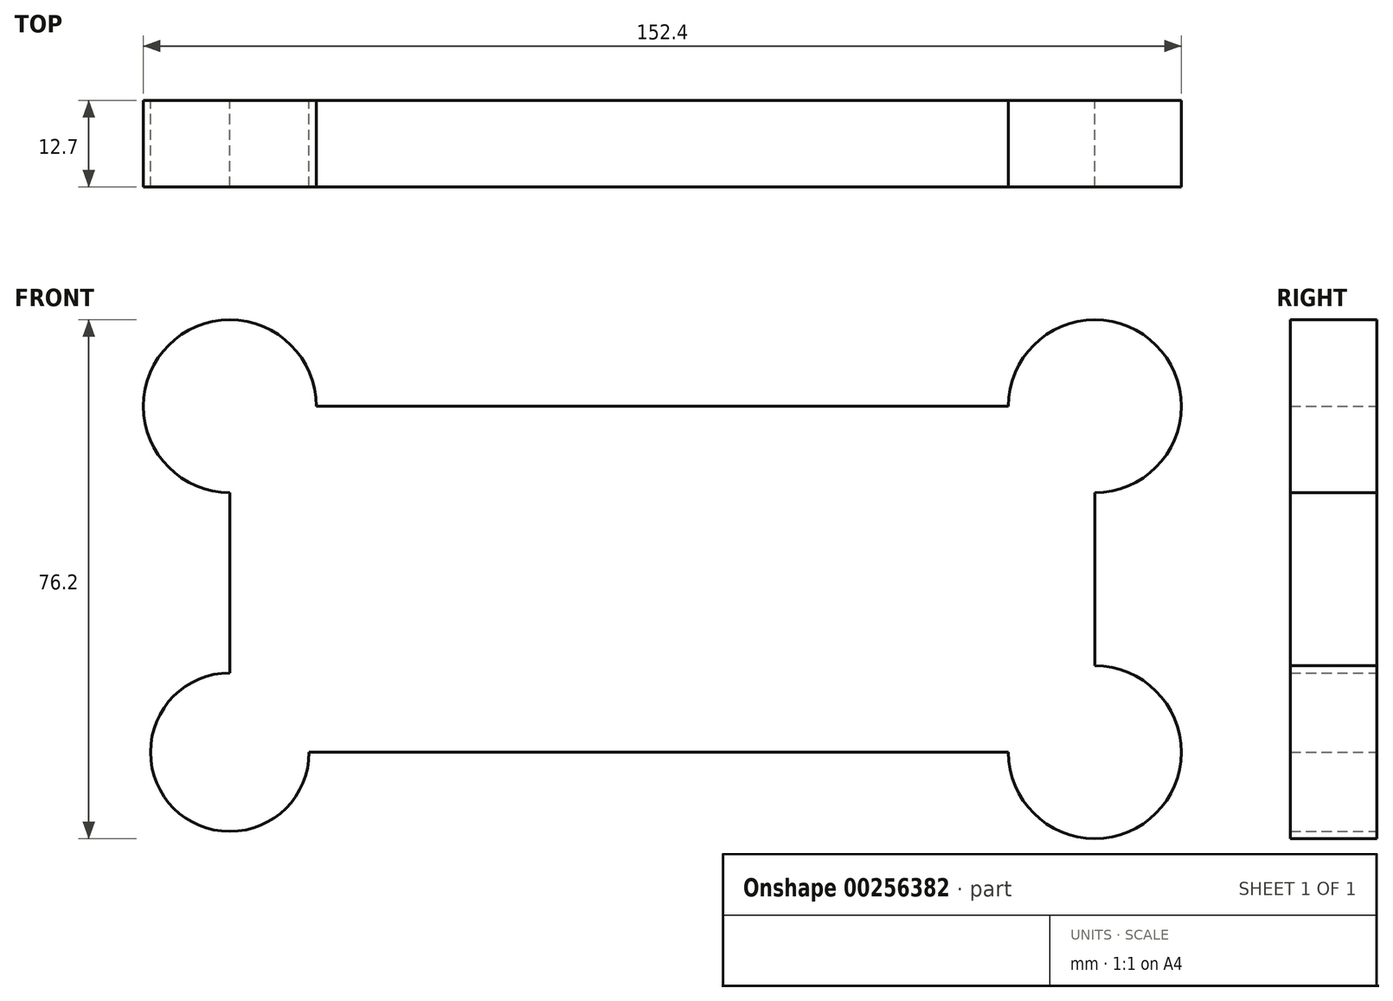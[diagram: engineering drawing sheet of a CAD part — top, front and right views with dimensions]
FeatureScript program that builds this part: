
annotation { "Feature Type Name" : "Feature", "Feature Type Description" : "" }
export const myFeature = defineFeature(function(context is Context, id is Id, definition is map)
    precondition{}
    {
        {
            var Q0;
            Q0=qCreatedBy(makeId("Front.planeOp"),FACE);
            var sketch = newSketch(context, id + "F0", { "sketchPlane" : qUnion([Q0])});
            skLineSegment(sketch, "E0.bottom", {"start": v(63.5, 25.4) * mm, "end": v(-63.5, 25.4) * mm});
            skLineSegment(sketch, "E0.top", {"start": v(63.5, -25.4) * mm, "end": v(-63.5, -25.4) * mm});
            skLineSegment(sketch, "E0.left", {"start": v(63.5, 25.4) * mm, "end": v(63.5, -25.4) * mm});
            skLineSegment(sketch, "E0.right", {"start": v(-63.5, 25.4) * mm, "end": v(-63.5, -25.4) * mm});
            skPoint(sketch, "E0.middle", {"position": v(0, 0) * mm});
            skCircle(sketch, "E1", {"center": v(-63.5, -25.4) * mm, "radius": 11.65 * mm});
            skCircle(sketch, "E2", {"center": v(-63.5, 25.4) * mm, "radius": 12.7 * mm});
            skCircle(sketch, "E3", {"center": v(63.5, 25.4) * mm, "radius": 12.7 * mm});
            skCircle(sketch, "E4", {"center": v(63.5, -25.4) * mm, "radius": 12.7 * mm});
            skSolve(sketch);
        }
        {
            var Q0;
            Q0 = qSketchRegion(id + "F0", true);
            extrude(context, id + "F1", {"entities" : qUnion([Q0]), "depth" : 12.7 * mm});
        }
    });
